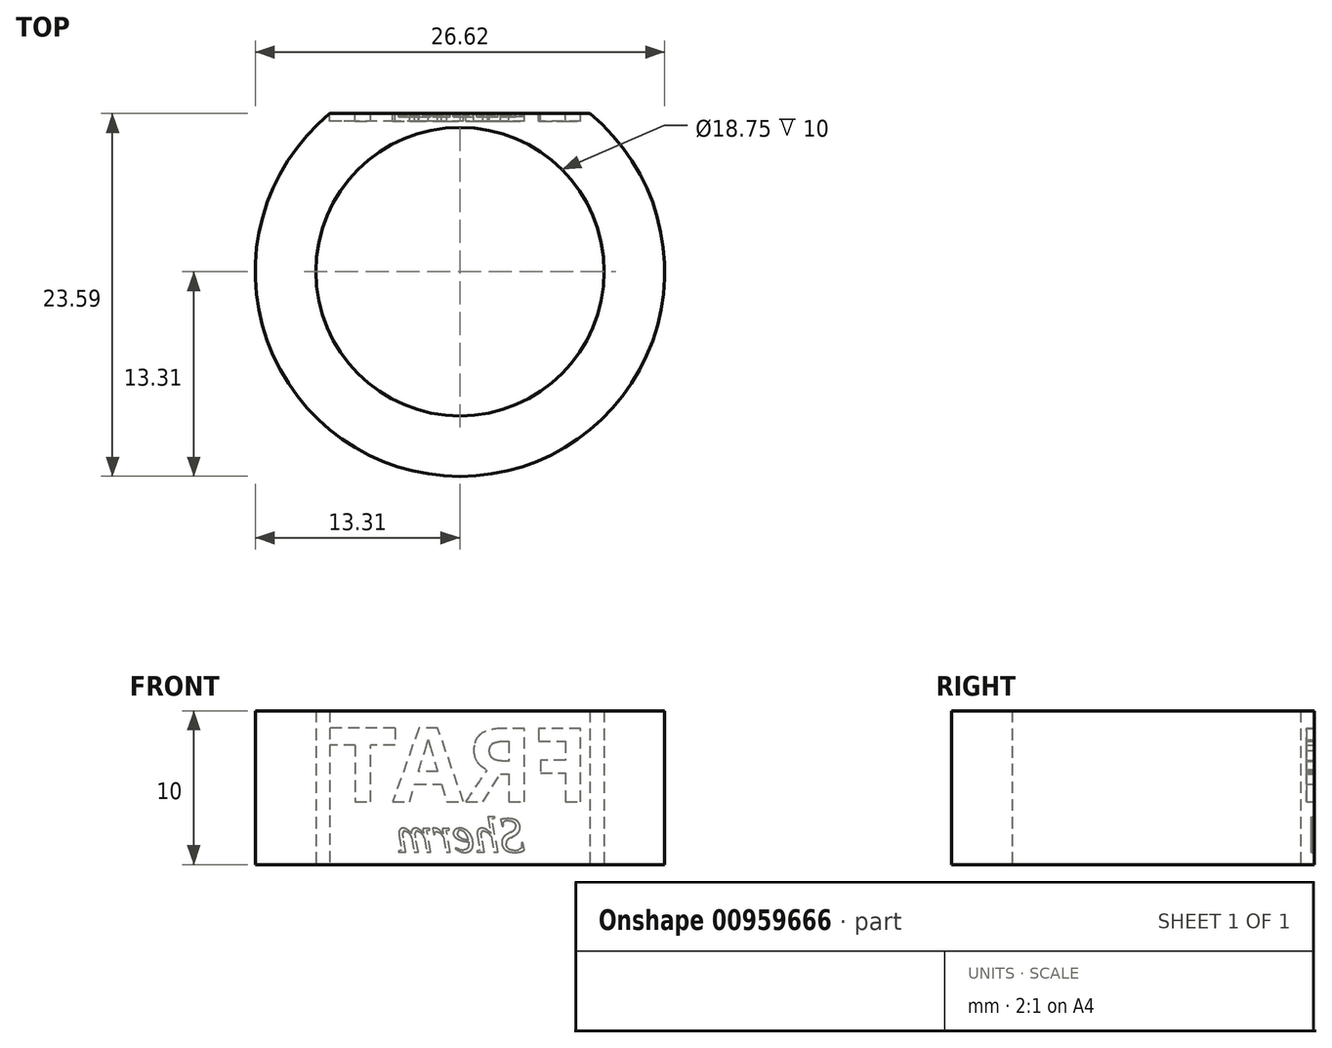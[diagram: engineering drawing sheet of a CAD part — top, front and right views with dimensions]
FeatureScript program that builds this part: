
annotation { "Feature Type Name" : "Feature", "Feature Type Description" : "" }
export const myFeature = defineFeature(function(context is Context, id is Id, definition is map)
    precondition{}
    {
        {
            var Q0;
            Q0=qCreatedBy(makeId("Top.planeOp"),FACE);
            var sketch = newSketch(context, id + "F0", { "sketchPlane" : qUnion([Q0])});
            skCircle(sketch, "E0", {"center": v(0, 0) * mm, "radius": 9.38 * mm});
            skCircle(sketch, "E1", {"center": v(0, 0) * mm, "radius": 13.31 * mm});
            skLineSegment(sketch, "E2", {"start": v(-8.46, 10.28) * mm, "end": v(8.46, 10.28) * mm});
            skSolve(sketch);
        }
        {
            var Q0;
            Q0=makeQuery(id+"F0.imprint","IMPRINT",FACE,{"disambiguationData":[TD([[makeQuery(id+"F0.imprint","IMPRINT",EDGE,{"derivedFrom":sQuery(id+"F0.wireOp",EDGE,"E0")}),-1.0]])]});
            extrude(context, id + "F1", {"entities" : qUnion([Q0]), "depth" : 10 * mm, "offsetDistance" : 25.4 * mm});
        }
        {
            var Q0;
            Q0=makeQuery(id+"F1.opExtrude","SWEPT_FACE",FACE,{"disambiguationData":[OSD([sQuery(id+"F0.wireOp",EDGE,"E2")])]});
            var sketch = newSketch(context, id + "F2", { "sketchPlane" : qUnion([Q0])});
            skLineSegment(sketch, "E3", {"start": v(-8.46, 7.78) * mm, "end": v(8.46, 7.78) * mm});
            skLineSegment(sketch, "E4", {"start": v(0, 7.78) * mm, "end": v(0, 10) * mm});
            skLineSegment(sketch, "E5", {"start": v(0, 8.9) * mm, "end": v(-8.46, 8.9) * mm});
            skLineSegment(sketch, "E6", {"start": v(-4.23, 8.9) * mm, "end": v(-4.23, 10) * mm});
            skLineSegment(sketch, "E7", {"start": v(-4.23, 10) * mm, "end": v(-4.23, 7.78) * mm});
            skLineSegment(sketch, "E8.MirrorCS", {"start": v(4.23, 10) * mm, "end": v(4.23, 7.78) * mm});
            skText(sketch, "E9", { "text": "FRAT", "fontName": "OpenSans-Bold.ttf"});
            skLineSegment(sketch, "E10", {"start": v(4.23, 8.9) * mm, "end": v(8.54, 8.9) * mm});
            skLineSegment(sketch, "E11", {"start": v(8.46, 7.78) * mm, "end": v(8.46, 8.9) * mm});
            const initialGuessF2  = {"E9": [-0.00846, 0.00408, 1, 0, 0.00481]};
            skSetInitialGuess(sketch, initialGuessF2);
            skSolve(sketch);
        }
        {
            var Q0;
            {var subQ8=sQuery(id+"F2.wireOp",EDGE,"E9.sketch_text.stroke-43");Q0=makeQuery(id+"F2.imprint","IMPRINT",FACE,{"disambiguationData":[TD([[makeQuery(id+"F2.imprint","IMPRINT",EDGE,{"derivedFrom":subQ8}),1.0]])]});}
            var Q1;
            {var subQ5=sQuery(id+"F2.wireOp",EDGE,"E9.sketch_text.stroke-41");Q1=makeQuery(id+"F2.imprint","IMPRINT",FACE,{"disambiguationData":[TD([[makeQuery(id+"F2.imprint","IMPRINT",EDGE,{"derivedFrom":subQ5}),-1.0]])]});}
            var Q2;
            {var subQ0=sQuery(id+"F2.wireOp",EDGE,"E9.sketch_text.stroke-43");Q2=makeQuery(id+"F2.imprint","IMPRINT",FACE,{"disambiguationData":[TD([[makeQuery(id+"F2.imprint","IMPRINT",EDGE,{"derivedFrom":subQ0}),-1.0]])]});}
            var Q3;
            Q3=makeQuery(id+"F2.imprint","IMPRINT",FACE,{"disambiguationData":[TD([[makeQuery(id+"F2.imprint","IMPRINT",EDGE,{"derivedFrom":sQuery(id+"F2.wireOp",EDGE,"E9.sketch_text.stroke-29")}),-1.0]])]});
            var Q4;
            {var subQ0=sQuery(id+"F2.wireOp",EDGE,"E9.sketch_text.stroke-34");Q4=makeQuery(id+"F2.imprint","IMPRINT",FACE,{"disambiguationData":[TD([[makeQuery(id+"F2.imprint","IMPRINT",EDGE,{"derivedFrom":subQ0}),-1.0]])]});}
            var Q5;
            {var subQ2=sQuery(id+"F2.wireOp",EDGE,"E9.sketch_text.stroke-10");Q5=makeQuery(id+"F2.imprint","IMPRINT",FACE,{"disambiguationData":[TD([[makeQuery(id+"F2.imprint","IMPRINT",EDGE,{"derivedFrom":subQ2}),-1.0]])]});}
            var Q6;
            {var subQ0=sQuery(id+"F2.wireOp",EDGE,"E9.sketch_text.stroke-14");Q6=makeQuery(id+"F2.imprint","IMPRINT",FACE,{"disambiguationData":[TD([[makeQuery(id+"F2.imprint","IMPRINT",EDGE,{"derivedFrom":subQ0}),-1.0]])]});}
            var Q7;
            {var subQ0=sQuery(id+"F2.wireOp",EDGE,"E9.sketch_text.stroke-2");Q7=makeQuery(id+"F2.imprint","IMPRINT",FACE,{"disambiguationData":[TD([[makeQuery(id+"F2.imprint","IMPRINT",EDGE,{"derivedFrom":subQ0}),-1.0]])]});}
            var Q8;
            {var subQ1=sQuery(id+"F2.wireOp",EDGE,"E9.sketch_text.stroke-0");Q8=makeQuery(id+"F2.imprint","IMPRINT",FACE,{"disambiguationData":[TD([[makeQuery(id+"F2.imprint","IMPRINT",EDGE,{"derivedFrom":subQ1}),-1.0]])]});}
            extrude(context, id + "F3", {"entities" : qUnion([Q0, Q1, Q2, Q3, Q4, Q5, Q6, Q7, Q8]), "operationType" : NewBodyOperationType.REMOVE, "oppositeDirection" : true, "depth" : .5 * mm, "offsetDistance" : 25 * mm});
        }
        {
            var Q0;
            {var subQ0=sQuery(id+"F0.wireOp",EDGE,"E2");var subQ1=sQuery(id+"F0.wireOp",EDGE,"E1");Q0=makeQuery(id+"F3.boolean.opBoolean","SPLIT",FACE,{"disambiguationData":[TD([makeQuery(id+"F1.opExtrude","SWEPT_FACE",FACE,{"disambiguationData":[OSD([subQ1])]})])],"derivedFrom":makeQuery(id+"F1.opExtrude","SWEPT_FACE",FACE,{"disambiguationData":[OSD([subQ0])]})});}
            var sketch = newSketch(context, id + "F4", { "sketchPlane" : qUnion([Q0])});
            skLineSegment(sketch, "E12", {"start": v(0, 0) * mm, "end": v(-8.46, 0) * mm});
            skLineSegment(sketch, "E13", {"start": v(-4.23, 0) * mm, "end": v(-4.23, 2.16) * mm});
            skLineSegment(sketch, "E14.MirrorCS", {"start": v(4.23, 0) * mm, "end": v(4.23, 2.16) * mm});
            skLineSegment(sketch, "E15.bottom", {"start": v(-4.23, 3.18) * mm, "end": v(4.23, 3.18) * mm});
            skLineSegment(sketch, "E15.top", {"start": v(-4.23, 0.82) * mm, "end": v(4.23, 0.82) * mm});
            skLineSegment(sketch, "E15.left", {"start": v(-4.23, 3.18) * mm, "end": v(-4.23, 0.82) * mm});
            skLineSegment(sketch, "E15.right", {"start": v(4.23, 3.18) * mm, "end": v(4.23, 0.82) * mm});
            skText(sketch, "E16", { "text": "Sherm", "fontName": "Tinos-Italic.ttf"});
            const initialGuessF4  = {"E16": [-0.00423, 0.00082, 1, 0, 0.00236]};
            skSetInitialGuess(sketch, initialGuessF4);
            skSolve(sketch);
        }
        {
            var Q0;
            Q0=makeQuery(id+"F4.imprint","IMPRINT",FACE,{"disambiguationData":[TD([[makeQuery(id+"F4.imprint","IMPRINT",EDGE,{"derivedFrom":sQuery(id+"F4.wireOp",EDGE,"E16.sketch_text.stroke-0")}),-1.0]])]});
            var Q1;
            {var subQ0=sQuery(id+"F4.wireOp",EDGE,"E16.sketch_text.stroke-32");var subQ1=sQuery(id+"F4.wireOp",EDGE,"E15.top");var subQ2=makeQuery(id+"F4.imprint","INTERSECT",VERTEX,{"derivedFrom":[subQ1,subQ0]});Q1=makeQuery(id+"F4.imprint","IMPRINT",FACE,{"disambiguationData":[TD([[makeQuery(id+"F4.imprint","IMPRINT",EDGE,{"disambiguationData":[TD([[subQ2,-1.0]])],"derivedFrom":subQ1}),-1.0]])]});}
            var Q2;
            {var subQ0=sQuery(id+"F4.wireOp",EDGE,"E16.sketch_text.stroke-68");var subQ1=sQuery(id+"F4.wireOp",EDGE,"E15.top");var subQ2=makeQuery(id+"F4.imprint","INTERSECT",VERTEX,{"derivedFrom":[subQ1,subQ0]});Q2=makeQuery(id+"F4.imprint","IMPRINT",FACE,{"disambiguationData":[TD([[makeQuery(id+"F4.imprint","IMPRINT",EDGE,{"disambiguationData":[TD([[subQ2,-1.0]])],"derivedFrom":subQ1}),-1.0]])]});}
            var Q3;
            Q3=makeQuery(id+"F4.imprint","IMPRINT",FACE,{"disambiguationData":[TD([[makeQuery(id+"F4.imprint","IMPRINT",EDGE,{"derivedFrom":sQuery(id+"F4.wireOp",EDGE,"E16.sketch_text.stroke-82")}),-1.0]])]});
            var Q4;
            Q4=makeQuery(id+"F4.imprint","IMPRINT",FACE,{"disambiguationData":[TD([[makeQuery(id+"F4.imprint","IMPRINT",EDGE,{"derivedFrom":sQuery(id+"F4.wireOp",EDGE,"E16.sketch_text.stroke-58")}),-1.0]])]});
            var Q5;
            Q5=makeQuery(id+"F4.imprint","IMPRINT",FACE,{"disambiguationData":[TD([[makeQuery(id+"F4.imprint","IMPRINT",EDGE,{"derivedFrom":sQuery(id+"F4.wireOp",EDGE,"E16.sketch_text.stroke-35")}),-1.0]])]});
            var Q6;
            Q6=makeQuery(id+"F4.imprint","IMPRINT",FACE,{"disambiguationData":[TD([[makeQuery(id+"F4.imprint","IMPRINT",EDGE,{"derivedFrom":sQuery(id+"F4.wireOp",EDGE,"E16.sketch_text.stroke-97")}),-1.0]])]});
            extrude(context, id + "F5", {"entities" : qUnion([Q0, Q1, Q2, Q3, Q4, Q5, Q6]), "operationType" : NewBodyOperationType.REMOVE, "oppositeDirection" : true, "depth" : .2 * mm, "offsetDistance" : 25 * mm});
        }
    });
